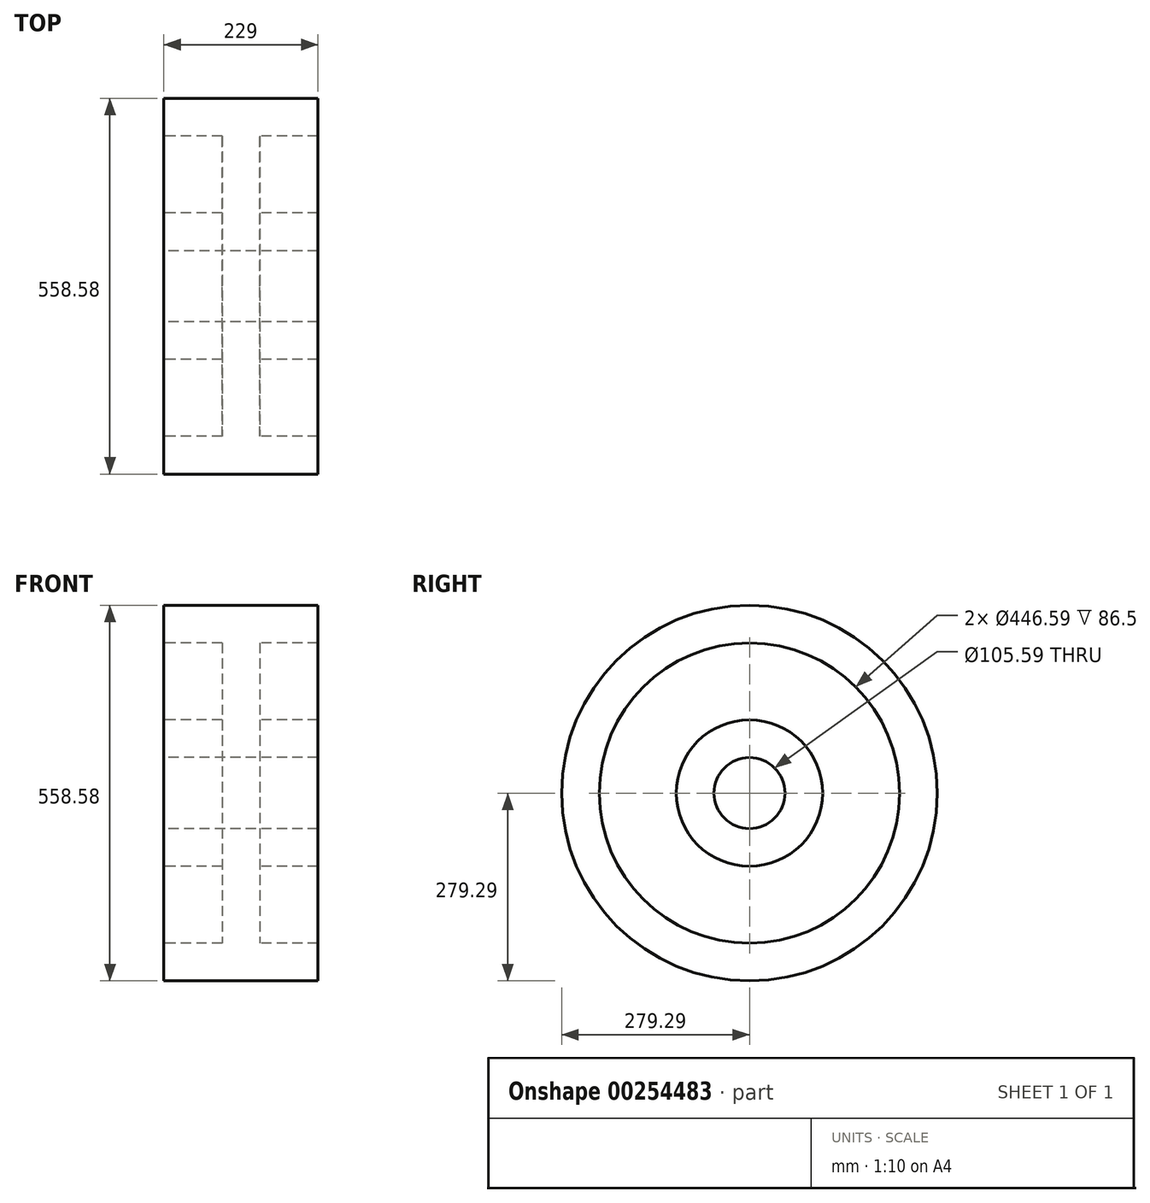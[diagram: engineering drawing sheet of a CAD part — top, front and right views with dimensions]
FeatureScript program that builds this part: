
annotation { "Feature Type Name" : "Feature", "Feature Type Description" : "" }
export const myFeature = defineFeature(function(context is Context, id is Id, definition is map)
    precondition{}
    {
        {
            var Q0;
            Q0=qCreatedBy(makeId("Front.planeOp"),FACE);
            var sketch = newSketch(context, id + "F0", { "sketchPlane" : qUnion([Q0])});
            skLineSegment(sketch, "E0", {"start": v(-122.5, 0) * mm, "end": v(122.5, 0) * mm, "construction": true});
            skLineSegment(sketch, "E1", {"start": v(-114.5, 279.3) * mm, "end": v(-114.5, 223.3) * mm});
            skLineSegment(sketch, "E2", {"start": v(-114.5, 279.3) * mm, "end": v(114.5, 279.3) * mm});
            skLineSegment(sketch, "E3", {"start": v(114.5, 279.3) * mm, "end": v(114.5, 223.3) * mm});
            skLineSegment(sketch, "E4", {"start": v(-114.5, 223.3) * mm, "end": v(-28, 223.3) * mm});
            skLineSegment(sketch, "E5", {"start": v(-28, 223.3) * mm, "end": v(-28, 108.8) * mm});
            skLineSegment(sketch, "E6", {"start": v(-28, 108.8) * mm, "end": v(-114.5, 108.8) * mm});
            skLineSegment(sketch, "E7", {"start": v(-114.5, 108.8) * mm, "end": v(-114.5, 52.8) * mm});
            skLineSegment(sketch, "E8", {"start": v(-114.5, 52.8) * mm, "end": v(114.5, 52.8) * mm});
            skLineSegment(sketch, "E9", {"start": v(114.5, 52.8) * mm, "end": v(114.5, 108.8) * mm});
            skLineSegment(sketch, "E10", {"start": v(28, 108.8) * mm, "end": v(28, 223.3) * mm});
            skLineSegment(sketch, "E11", {"start": v(28, 108.8) * mm, "end": v(114.5, 108.8) * mm});
            skLineSegment(sketch, "E12", {"start": v(28, 223.3) * mm, "end": v(114.5, 223.3) * mm});
            skLineSegment(sketch, "E13", {"start": v(0, 0) * mm, "end": v(0, 292.3) * mm, "construction": true});
            skPoint(sketch, "E13.endSnap0", {"position": v(0, 0) * mm});
            skSolve(sketch);
        }
        {
            var Q0;
            Q0=qSketchRegion(id+"F0",true);
            var Q1;
            Q1=sQuery(id+"F0.wireOp",EDGE,"E0");
            revolve(context, id + "F1", {"entities" : qUnion([Q0]), "axis" : qUnion([Q1]), "revolveType" : RevolveType.FULL});
        }
    });
